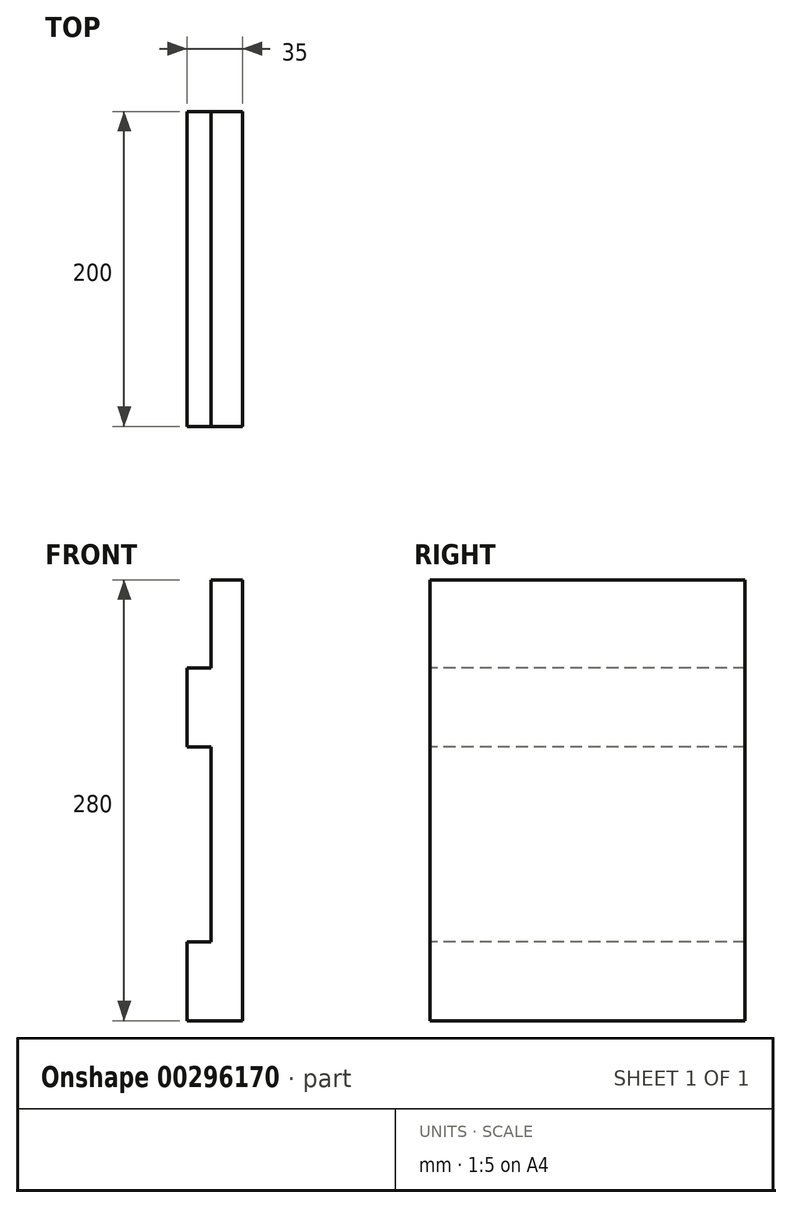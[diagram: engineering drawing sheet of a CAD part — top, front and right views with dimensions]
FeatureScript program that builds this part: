
annotation { "Feature Type Name" : "Feature", "Feature Type Description" : "" }
export const myFeature = defineFeature(function(context is Context, id is Id, definition is map)
    precondition{}
    {
        {
            var Q0;
            Q0=qCreatedBy(makeId("Front.planeOp"),FACE);
            var sketch = newSketch(context, id + "F0", { "sketchPlane" : qUnion([Q0])});
            skLineSegment(sketch, "E0.bottom", {"start": v(-28.35, -31.5) * mm, "end": v(-48.35, -31.5) * mm});
            skLineSegment(sketch, "E0.top", {"start": v(-28.35, 248.5) * mm, "end": v(-48.35, 248.5) * mm});
            skLineSegment(sketch, "E0.left", {"start": v(-28.35, -31.5) * mm, "end": v(-28.35, 248.5) * mm});
            skLineSegment(sketch, "E0.right", {"start": v(-48.35, -31.5) * mm, "end": v(-48.35, 248.5) * mm});
            skPoint(sketch, "E0.middle", {"position": v(-38.35, 108.5) * mm});
            skSolve(sketch);
        }
        {
            var Q0;
            Q0=makeQuery(id+"F0.imprint","IMPRINT",FACE,{"disambiguationData":[TD([[makeQuery(id+"F0.imprint","IMPRINT",EDGE,{"derivedFrom":sQuery(id+"F0.wireOp",EDGE,"E0.bottom")}),-1.0]])]});
            extrude(context, id + "F1", {"entities" : qUnion([Q0]), "oppositeDirection" : true, "depth" : 200 * mm});
        }
        {
            var Q0;
            Q0=makeQuery(id+"F1.opExtrude","CAP_FACE",FACE,{"disambiguationData":[OSD([sQuery(id+"F0.wireOp",EDGE,"E0.bottom"),sQuery(id+"F0.wireOp",EDGE,"E0.top"),sQuery(id+"F0.wireOp",EDGE,"E0.left"),sQuery(id+"F0.wireOp",EDGE,"E0.right")])],"isStart":true});
            var sketch = newSketch(context, id + "F2", { "sketchPlane" : qUnion([Q0])});
            skLineSegment(sketch, "E1.bottom", {"start": v(-48.35, 142.5) * mm, "end": v(-63.35, 142.5) * mm});
            skLineSegment(sketch, "E1.top", {"start": v(-48.35, 192.5) * mm, "end": v(-63.35, 192.5) * mm});
            skLineSegment(sketch, "E1.left", {"start": v(-48.35, 142.5) * mm, "end": v(-48.35, 192.5) * mm});
            skLineSegment(sketch, "E1.right", {"start": v(-63.35, 142.5) * mm, "end": v(-63.35, 192.5) * mm});
            skPoint(sketch, "E1.middle", {"position": v(-55.85, 167.5) * mm});
            skLineSegment(sketch, "E2.bottom", {"start": v(-48.35, -31.5) * mm, "end": v(-63.35, -31.5) * mm});
            skLineSegment(sketch, "E2.top", {"start": v(-48.35, 18.5) * mm, "end": v(-63.35, 18.5) * mm});
            skLineSegment(sketch, "E2.left", {"start": v(-48.35, -31.5) * mm, "end": v(-48.35, 18.5) * mm});
            skLineSegment(sketch, "E2.right", {"start": v(-63.35, -31.5) * mm, "end": v(-63.35, 18.5) * mm});
            skPoint(sketch, "E2.middle", {"position": v(-55.85, -6.5) * mm});
            skSolve(sketch);
        }
        {
            var Q0;
            Q0=makeQuery(id+"F2.imprint","IMPRINT",FACE,{"disambiguationData":[TD([[makeQuery(id+"F2.imprint","IMPRINT",EDGE,{"derivedFrom":sQuery(id+"F2.wireOp",EDGE,"E1.bottom")}),-1.0]])]});
            var Q1;
            Q1=makeQuery(id+"F2.imprint","IMPRINT",FACE,{"disambiguationData":[TD([[makeQuery(id+"F2.imprint","IMPRINT",EDGE,{"derivedFrom":sQuery(id+"F2.wireOp",EDGE,"E2.bottom")}),-1.0]])]});
            extrude(context, id + "F3", {"entities" : qUnion([Q0, Q1]), "operationType" : NewBodyOperationType.ADD, "oppositeDirection" : true, "depth" : 200 * mm});
        }
    });
